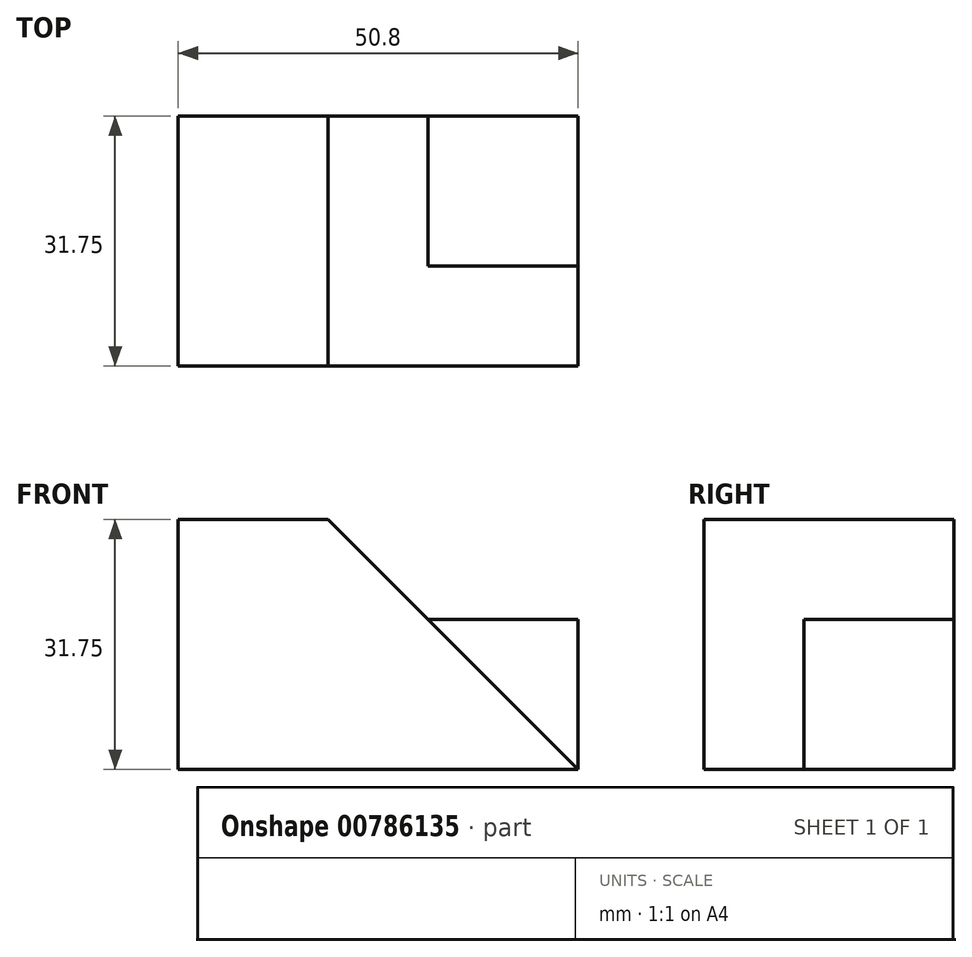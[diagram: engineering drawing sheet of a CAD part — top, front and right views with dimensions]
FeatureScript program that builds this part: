
annotation { "Feature Type Name" : "Feature", "Feature Type Description" : "" }
export const myFeature = defineFeature(function(context is Context, id is Id, definition is map)
    precondition{}
    {
        {
            var Q0;
            Q0=qCreatedBy(makeId("Front.planeOp"),FACE);
            var sketch = newSketch(context, id + "F0", { "sketchPlane" : qUnion([Q0])});
            skLineSegment(sketch, "E0", {"start": v(0, 0) * mm, "end": v(0, 31.75) * mm});
            skLineSegment(sketch, "E1", {"start": v(0, 31.75) * mm, "end": v(19.05, 31.75) * mm});
            skLineSegment(sketch, "E2", {"start": v(0, 0) * mm, "end": v(50.8, 0) * mm});
            skLineSegment(sketch, "E3", {"start": v(19.05, 31.75) * mm, "end": v(50.8, 0) * mm});
            skSolve(sketch);
        }
        {
            var Q0;
            Q0 = qSketchRegion(id + "F0", true);
            extrude(context, id + "F1", {"entities" : qUnion([Q0]), "depth" : 31.75 * mm, "offsetDistance" : 25.4 * mm});
        }
        {
            var Q0;
            Q0=makeQuery(id+"F1.opExtrude","CAP_FACE",FACE,{"disambiguationData":[OSD([sQuery(id+"F0.wireOp",EDGE,"E0"),sQuery(id+"F0.wireOp",EDGE,"E1"),sQuery(id+"F0.wireOp",EDGE,"E2"),sQuery(id+"F0.wireOp",EDGE,"E3")])],"isStart":false});
            var sketch = newSketch(context, id + "F2", { "sketchPlane" : qUnion([Q0])});
            skLineSegment(sketch, "E4", {"start": v(50.8, 0) * mm, "end": v(50.8, 19.05) * mm});
            skLineSegment(sketch, "E5", {"start": v(50.8, 19.05) * mm, "end": v(31.75, 19.05) * mm});
            skLineSegment(sketch, "E6", {"start": v(31.75, 19.05) * mm, "end": v(50.8, 0) * mm});
            skSolve(sketch);
        }
        {
            var Q0;
            Q0 = qSketchRegion(id + "F2", true);
            extrude(context, id + "F3", {"entities" : qUnion([Q0]), "depth" : 19.05 * mm, "offsetDistance" : 25.4 * mm});
        }
        {
            var Q0;
            Q0=makeQuery(id+"F3.opExtrude","SWEPT_BODY",BODY,{"disambiguationData":[OSD([sQuery(id+"F2.wireOp",EDGE,"E4"),sQuery(id+"F2.wireOp",EDGE,"E5"),sQuery(id+"F2.wireOp",EDGE,"E6")])]});
            transform(context, id + "F4", {"entities" : qUnion([Q0]), "transformType" : TransformType.TRANSLATION_3D, "dx" : 0 * mm, "dy" : 31.75 * mm, "dz" : 0 * mm, "makeCopy" : false});
        }
    });
